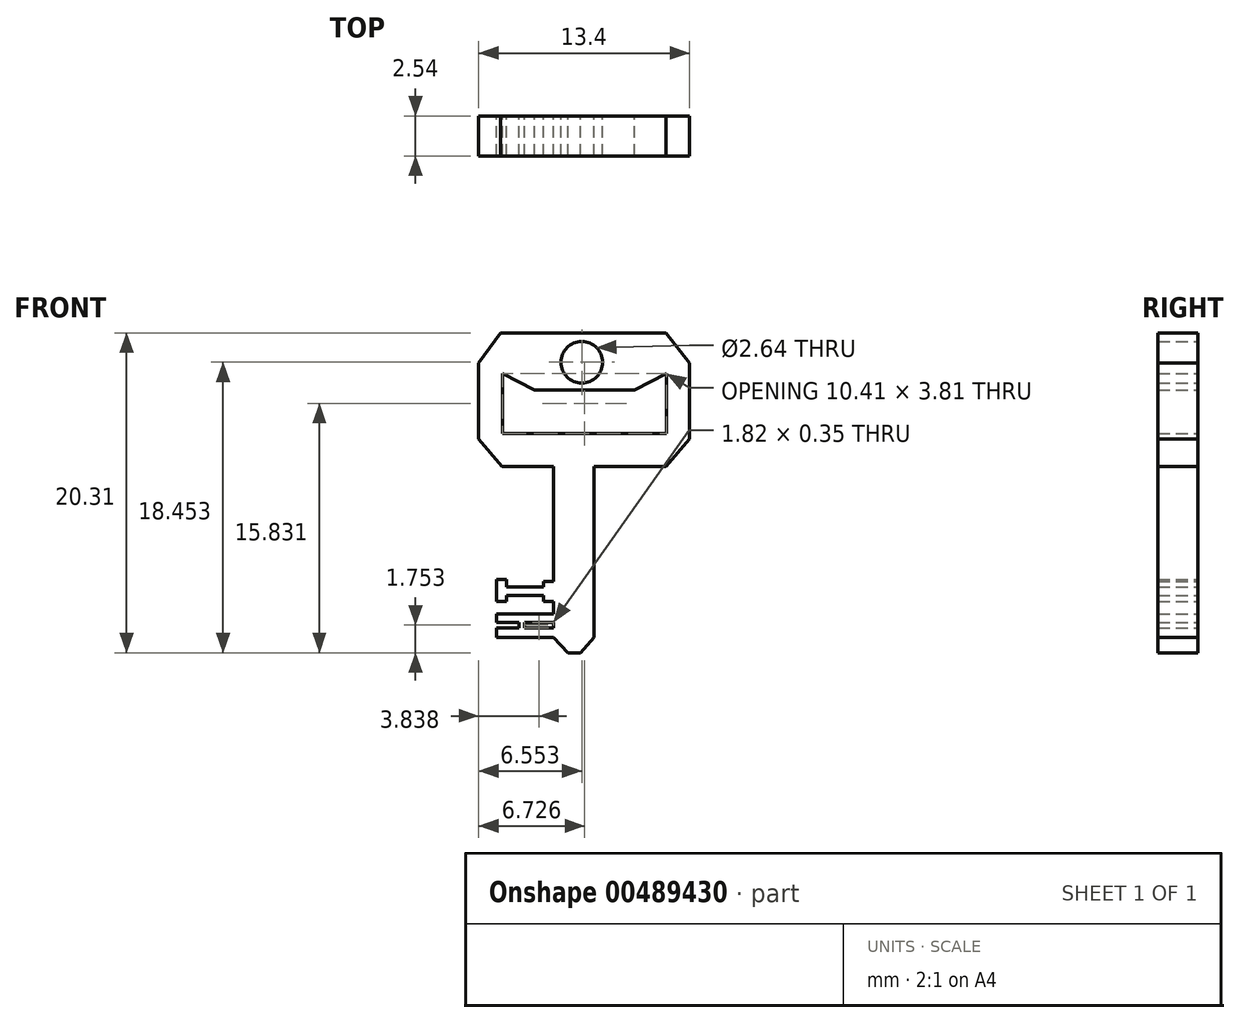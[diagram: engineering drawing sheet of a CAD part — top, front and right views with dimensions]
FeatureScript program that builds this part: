
annotation { "Feature Type Name" : "Feature", "Feature Type Description" : "" }
export const myFeature = defineFeature(function(context is Context, id is Id, definition is map)
    precondition{}
    {
        {
            var Q0;
            Q0=qCreatedBy(makeId("Front.planeOp"),FACE);
            var sketch = newSketch(context, id + "F0", { "sketchPlane" : qUnion([Q0])});
            skLineSegment(sketch, "E0", {"start": v(8.47, 22.9) * mm, "end": v(18.97, 22.9) * mm});
            skLineSegment(sketch, "E1", {"start": v(18.97, 22.9) * mm, "end": v(20.47, 21.01) * mm});
            skLineSegment(sketch, "E2", {"start": v(20.47, 21.01) * mm, "end": v(20.47, 16.19) * mm});
            skLineSegment(sketch, "E3", {"start": v(20.47, 16.19) * mm, "end": v(18.97, 14.44) * mm});
            skLineSegment(sketch, "E4", {"start": v(18.97, 14.44) * mm, "end": v(8.57, 14.44) * mm});
            skLineSegment(sketch, "E5", {"start": v(8.57, 14.44) * mm, "end": v(7.07, 16.19) * mm});
            skLineSegment(sketch, "E6", {"start": v(7.07, 16.19) * mm, "end": v(7.07, 21.01) * mm});
            skLineSegment(sketch, "E7", {"start": v(7.07, 21.01) * mm, "end": v(8.47, 22.9) * mm});
            skCircle(sketch, "E8", {"center": v(13.62, 21.05) * mm, "radius": 1.32 * mm});
            skLineSegment(sketch, "E9", {"start": v(11.82, 3.57) * mm, "end": v(12.74, 2.6) * mm});
            skLineSegment(sketch, "E10", {"start": v(11.82, 5.06) * mm, "end": v(8.21, 5.06) * mm});
            skLineSegment(sketch, "E11", {"start": v(8.21, 5.06) * mm, "end": v(8.21, 4.53) * mm});
            skLineSegment(sketch, "E12", {"start": v(11.82, 3.57) * mm, "end": v(8.21, 3.57) * mm});
            skLineSegment(sketch, "E13", {"start": v(8.21, 4.53) * mm, "end": v(9.63, 4.53) * mm});
            skLineSegment(sketch, "E14", {"start": v(11.82, 4.53) * mm, "end": v(10, 4.53) * mm});
            skLineSegment(sketch, "E15", {"start": v(10, 4.53) * mm, "end": v(10, 4.18) * mm});
            skLineSegment(sketch, "E16", {"start": v(9.63, 4.53) * mm, "end": v(9.63, 4.18) * mm});
            skLineSegment(sketch, "E17", {"start": v(9.63, 4.18) * mm, "end": v(8.21, 4.18) * mm});
            skLineSegment(sketch, "E18", {"start": v(8.21, 4.18) * mm, "end": v(8.21, 3.57) * mm});
            skLineSegment(sketch, "E19", {"start": v(10, 4.18) * mm, "end": v(11.82, 4.18) * mm});
            skLineSegment(sketch, "E20", {"start": v(11.82, 3.57) * mm, "end": v(11.82, 4.18) * mm});
            skLineSegment(sketch, "E21", {"start": v(11.82, 4.53) * mm, "end": v(11.82, 5.06) * mm});
            skLineSegment(sketch, "E22", {"start": v(11.82, 5.86) * mm, "end": v(11.18, 5.86) * mm});
            skLineSegment(sketch, "E23", {"start": v(11.18, 7.13) * mm, "end": v(11.82, 7.13) * mm});
            skLineSegment(sketch, "E24", {"start": v(8.21, 5.86) * mm, "end": v(8.85, 5.86) * mm});
            skLineSegment(sketch, "E25", {"start": v(8.21, 7.24) * mm, "end": v(8.85, 7.24) * mm});
            skLineSegment(sketch, "E26", {"start": v(8.21, 5.86) * mm, "end": v(8.21, 7.24) * mm});
            skLineSegment(sketch, "E27", {"start": v(11.18, 6.25) * mm, "end": v(8.85, 6.25) * mm});
            skLineSegment(sketch, "E28", {"start": v(8.85, 6.8) * mm, "end": v(11.18, 6.8) * mm});
            skLineSegment(sketch, "E29", {"start": v(11.18, 6.25) * mm, "end": v(11.18, 5.86) * mm});
            skLineSegment(sketch, "E30", {"start": v(11.18, 6.8) * mm, "end": v(11.18, 7.13) * mm});
            skLineSegment(sketch, "E31", {"start": v(8.85, 6.8) * mm, "end": v(8.85, 7.24) * mm});
            skLineSegment(sketch, "E32", {"start": v(8.85, 6.25) * mm, "end": v(8.85, 5.86) * mm});
            skLineSegment(sketch, "E33", {"start": v(11.82, 5.86) * mm, "end": v(11.82, 14.44) * mm});
            skLineSegment(sketch, "E34", {"start": v(12.74, 2.6) * mm, "end": v(13.55, 2.6) * mm});
            skLineSegment(sketch, "E35", {"start": v(14.4, 3.57) * mm, "end": v(13.55, 2.6) * mm});
            skLineSegment(sketch, "E36", {"start": v(14.4, 3.57) * mm, "end": v(14.4, 14.44) * mm});
            skLineSegment(sketch, "E37", {"start": v(8.59, 20.34) * mm, "end": v(10.62, 19.3) * mm});
            skLineSegment(sketch, "E38", {"start": v(10.62, 19.3) * mm, "end": v(16.97, 19.3) * mm});
            skLineSegment(sketch, "E39", {"start": v(19, 20.34) * mm, "end": v(16.97, 19.3) * mm});
            skLineSegment(sketch, "E40", {"start": v(19, 20.34) * mm, "end": v(19, 16.53) * mm});
            skLineSegment(sketch, "E41", {"start": v(19, 16.53) * mm, "end": v(8.59, 16.53) * mm});
            skLineSegment(sketch, "E42", {"start": v(8.59, 20.34) * mm, "end": v(8.59, 16.53) * mm});
            skLineSegment(sketch, "E43", {"start": v(11.82, 5.86) * mm, "end": v(11.82, 5.06) * mm});
            skLineSegment(sketch, "E44", {"start": v(11.82, 4.18) * mm, "end": v(11.82, 4.53) * mm});
            skSolve(sketch);
        }
        {
            var Q0;
            Q0=makeQuery(id+"F0.imprint","IMPRINT",FACE,{"disambiguationData":[TD([[makeQuery(id+"F0.imprint","IMPRINT",EDGE,{"derivedFrom":sQuery(id+"F0.wireOp",EDGE,"E0")}),-1.0]])]});
            var Q1;
            {var subQ0=sQuery(id+"F0.wireOp",EDGE,"E22");Q1=makeQuery(id+"F0.imprint","IMPRINT",FACE,{"disambiguationData":[TD([[makeQuery(id+"F0.imprint","IMPRINT",EDGE,{"derivedFrom":subQ0}),-1.0]])]});}
            var Q2;
            Q2=makeQuery(id+"F0.imprint","IMPRINT",FACE,{"disambiguationData":[TD([[makeQuery(id+"F0.imprint","IMPRINT",EDGE,{"derivedFrom":sQuery(id+"F0.wireOp",EDGE,"E10")}),1.0]])]});
            var Q3;
            Q3=makeQuery(id+"F0.imprint","IMPRINT",FACE,{"disambiguationData":[TD([[makeQuery(id+"F0.imprint","IMPRINT",EDGE,{"derivedFrom":sQuery(id+"F0.wireOp",EDGE,"E9")}),1.0]])]});
            extrude(context, id + "F1", {"entities" : qUnion([Q0, Q1, Q2, Q3]), "depth" : 2.54 * mm, "offsetDistance" : 25.4 * mm});
        }
    });
